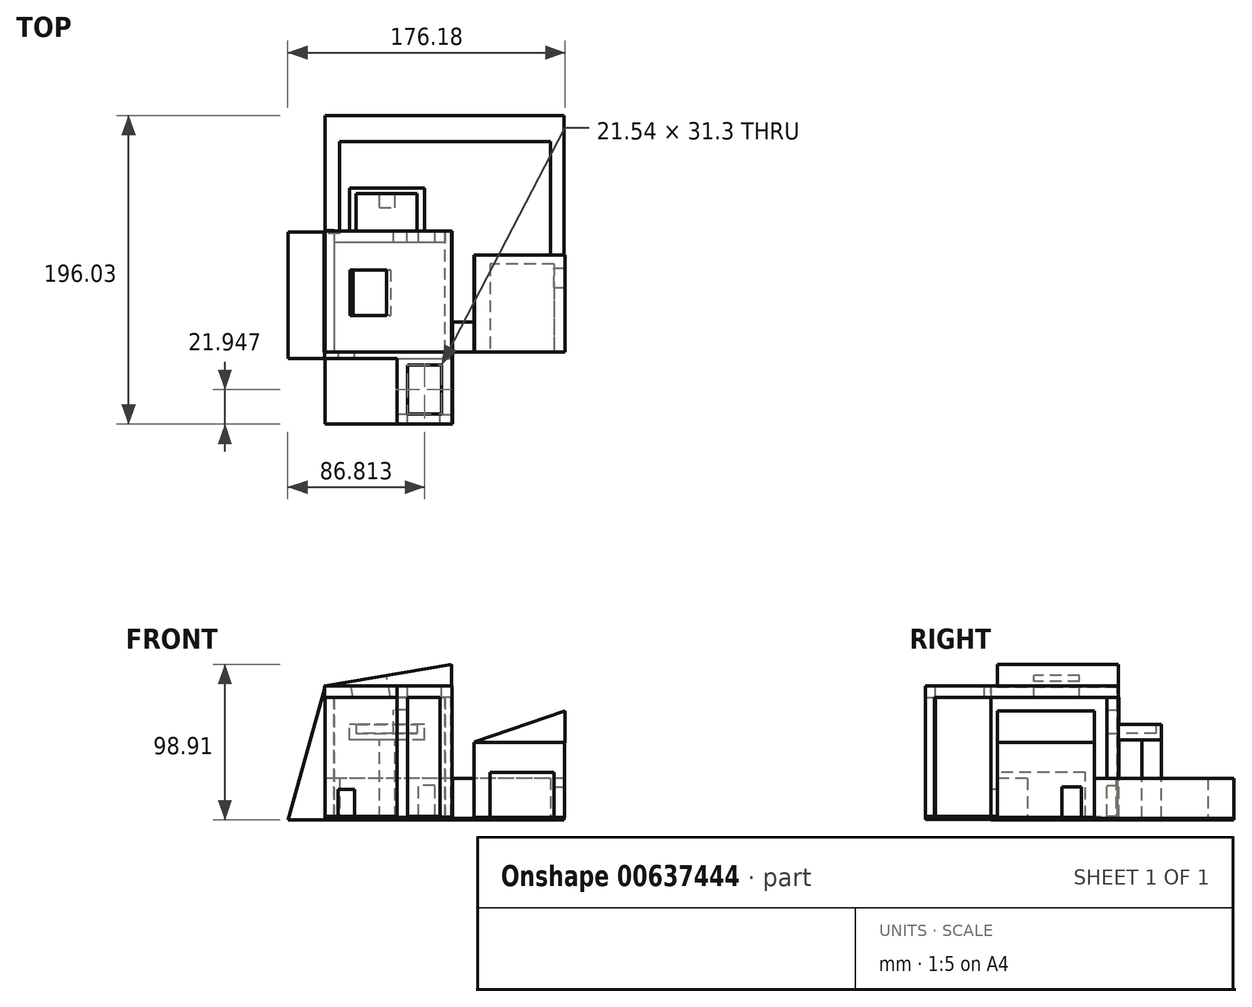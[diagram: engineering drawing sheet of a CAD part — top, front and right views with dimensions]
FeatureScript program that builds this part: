
annotation { "Feature Type Name" : "Feature", "Feature Type Description" : "" }
export const myFeature = defineFeature(function(context is Context, id is Id, definition is map)
    precondition{}
    {
        {
            var Q0;
            Q0=qCreatedBy(makeId("Front.planeOp"),FACE);
            var sketch = newSketch(context, id + "F0", { "sketchPlane" : qUnion([Q0])});
            skLineSegment(sketch, "E0.bottom", {"start": v(-75.95, -75.95) * mm, "end": v(21.4, -75.95) * mm});
            skLineSegment(sketch, "E0.top", {"start": v(-75.95, 0) * mm, "end": v(21.4, 0) * mm});
            skLineSegment(sketch, "E0.left", {"start": v(-75.95, -75.95) * mm, "end": v(-75.95, 0) * mm});
            skLineSegment(sketch, "E0.right", {"start": v(21.4, -75.95) * mm, "end": v(21.4, 0) * mm});
            skSolve(sketch);
        }
        {
            var Q0;
            Q0 = qSketchRegion(id + "F0", true);
            extrude(context, id + "F1", {"entities" : qUnion([Q0]), "depth" : 4.06 * mm, "offsetDistance" : 25.4 * mm});
        }
        {
            var Q0;
            Q0=qCreatedBy(makeId("Right.planeOp"),FACE);
            var sketch = newSketch(context, id + "F2", { "sketchPlane" : qUnion([Q0])});
            skLineSegment(sketch, "E1.bottom", {"start": v(0, 0) * mm, "end": v(76.87, 0) * mm});
            skLineSegment(sketch, "E1.top", {"start": v(0, -75.72) * mm, "end": v(76.87, -75.72) * mm});
            skLineSegment(sketch, "E1.left", {"start": v(0, 0) * mm, "end": v(0, -75.72) * mm});
            skLineSegment(sketch, "E1.right", {"start": v(76.87, 0) * mm, "end": v(76.87, -75.72) * mm});
            skSolve(sketch);
        }
        {
            var Q0;
            Q0=makeQuery(id+"F2.imprint","IMPRINT",FACE,{"disambiguationData":[TD([[makeQuery(id+"F2.imprint","IMPRINT",EDGE,{"derivedFrom":sQuery(id+"F2.wireOp",EDGE,"E1.bottom")}),-1.0]])]});
            extrude(context, id + "F3", {"entities" : qUnion([Q0]), "operationType" : NewBodyOperationType.ADD, "depth" : 4.06 * mm, "offsetDistance" : 25.4 * mm});
        }
        {
            var Q0;
            Q0=makeQuery(id+"F3.boolean.opBoolean","MERGE",FACE,{"derivedFrom":[makeQuery(id+"F1.opExtrude","SWEPT_FACE",FACE,{"disambiguationData":[OSD([sQuery(id+"F0.wireOp",EDGE,"E0.top")])]}),makeQuery(id+"F3.opExtrude","SWEPT_FACE",FACE,{"disambiguationData":[OSD([sQuery(id+"F2.wireOp",EDGE,"E1.bottom")])]})]});
            var sketch = newSketch(context, id + "F4", { "sketchPlane" : qUnion([Q0])});
            skLineSegment(sketch, "E2", {"start": v(4.06, 0) * mm, "end": v(4.06, -4.06) * mm});
            skLineSegment(sketch, "E3", {"start": v(4.06, -4.06) * mm, "end": v(21.4, -4.06) * mm});
            skLineSegment(sketch, "E4", {"start": v(21.4, -4.06) * mm, "end": v(21.4, 0) * mm});
            skLineSegment(sketch, "E5", {"start": v(21.4, 0) * mm, "end": v(4.06, 0) * mm});
            skSolve(sketch);
        }
        {
            var Q0;
            Q0=makeQuery(id+"F4.imprint","IMPRINT",FACE,{"disambiguationData":[TD([[makeQuery(id+"F4.imprint","IMPRINT",EDGE,{"derivedFrom":sQuery(id+"F4.wireOp",EDGE,"E2")}),1.0]])]});
            extrude(context, id + "F5", {"entities" : qUnion([Q0]), "operationType" : NewBodyOperationType.REMOVE, "oppositeDirection" : true, "depth" : 78.49 * mm, "offsetDistance" : 25.4 * mm});
        }
        {
            var Q0;
            Q0=qCreatedBy(makeId("Top.planeOp"),FACE);
            var sketch = newSketch(context, id + "F6", { "sketchPlane" : qUnion([Q0])});
            skLineSegment(sketch, "E6.bottom", {"start": v(4.07, 76.9) * mm, "end": v(-76, 76.9) * mm});
            skLineSegment(sketch, "E6.top", {"start": v(4.07, 69.6) * mm, "end": v(-76, 69.6) * mm});
            skLineSegment(sketch, "E6.left", {"start": v(4.07, 76.9) * mm, "end": v(4.07, 69.6) * mm});
            skLineSegment(sketch, "E6.right", {"start": v(-76, 76.9) * mm, "end": v(-76, 69.6) * mm});
            skSolve(sketch);
        }
        {
            var Q0;
            Q0=makeQuery(id+"F6.imprint","IMPRINT",FACE,{"disambiguationData":[TD([[makeQuery(id+"F6.imprint","IMPRINT",EDGE,{"derivedFrom":sQuery(id+"F6.wireOp",EDGE,"E6.bottom")}),1.0]])]});
            extrude(context, id + "F7", {"entities" : qUnion([Q0]), "operationType" : NewBodyOperationType.ADD, "oppositeDirection" : true, "depth" : 75.44 * mm, "offsetDistance" : 25.4 * mm});
        }
        {
            var Q0;
            Q0=makeQuery(id+"F1.opExtrude","CAP_FACE",FACE,{"disambiguationData":[OSD([sQuery(id+"F0.wireOp",EDGE,"E0.bottom"),sQuery(id+"F0.wireOp",EDGE,"E0.top"),sQuery(id+"F0.wireOp",EDGE,"E0.left"),sQuery(id+"F0.wireOp",EDGE,"E0.right")])],"isStart":false});
            var sketch = newSketch(context, id + "F8", { "sketchPlane" : qUnion([Q0])});
            skLineSegment(sketch, "E7.bottom", {"start": v(-67.84, -75.95) * mm, "end": v(-57.2, -75.95) * mm});
            skLineSegment(sketch, "E7.top", {"start": v(-67.84, -58.33) * mm, "end": v(-57.2, -58.33) * mm});
            skLineSegment(sketch, "E7.left", {"start": v(-67.84, -75.95) * mm, "end": v(-67.84, -58.33) * mm});
            skLineSegment(sketch, "E7.right", {"start": v(-57.2, -75.95) * mm, "end": v(-57.2, -58.33) * mm});
            skSolve(sketch);
        }
        {
            var Q0;
            Q0=makeQuery(id+"F8.imprint","IMPRINT",FACE,{"disambiguationData":[TD([[makeQuery(id+"F8.imprint","IMPRINT",EDGE,{"derivedFrom":sQuery(id+"F8.wireOp",EDGE,"E7.bottom")}),1.0]])]});
            extrude(context, id + "F9", {"entities" : qUnion([Q0]), "operationType" : NewBodyOperationType.REMOVE, "oppositeDirection" : true, "depth" : 25.4 * mm, "offsetDistance" : 25.4 * mm});
        }
        {
            var Q0;
            Q0=qCreatedBy(makeId("Top.planeOp"),FACE);
            var sketch = newSketch(context, id + "F10", { "sketchPlane" : qUnion([Q0])});
            skLineSegment(sketch, "E8.bottom", {"start": v(-76.3, 77.21) * mm, "end": v(-70.4, 77.21) * mm});
            skLineSegment(sketch, "E8.top", {"start": v(-76.3, -3.73) * mm, "end": v(-70.4, -3.73) * mm});
            skLineSegment(sketch, "E8.left", {"start": v(-76.3, 77.21) * mm, "end": v(-76.3, -3.73) * mm});
            skLineSegment(sketch, "E8.right", {"start": v(-70.4, 77.21) * mm, "end": v(-70.4, -3.73) * mm});
            skSolve(sketch);
        }
        {
            var Q0;
            Q0=makeQuery(id+"F10.imprint","IMPRINT",FACE,{"disambiguationData":[TD([[makeQuery(id+"F10.imprint","IMPRINT",EDGE,{"derivedFrom":sQuery(id+"F10.wireOp",EDGE,"E8.bottom")}),-1.0]])]});
            extrude(context, id + "F11", {"entities" : qUnion([Q0]), "operationType" : NewBodyOperationType.ADD, "oppositeDirection" : true, "depth" : 75.95 * mm, "offsetDistance" : 25.4 * mm});
        }
        {
            var Q0;
            Q0=qCreatedBy(makeId("Top.planeOp"),FACE);
            var sketch = newSketch(context, id + "F12", { "sketchPlane" : qUnion([Q0])});
            skLineSegment(sketch, "E9.bottom", {"start": v(-76.23, 76.97) * mm, "end": v(4.6, 76.97) * mm});
            skLineSegment(sketch, "E9.top", {"start": v(-76.23, -4.14) * mm, "end": v(4.6, -4.14) * mm});
            skLineSegment(sketch, "E9.left", {"start": v(-76.23, 76.97) * mm, "end": v(-76.23, -4.14) * mm});
            skLineSegment(sketch, "E9.right", {"start": v(4.6, 76.97) * mm, "end": v(4.6, -4.14) * mm});
            skSolve(sketch);
        }
        {
            var Q0;
            Q0=makeQuery(id+"F12.imprint","IMPRINT",FACE,{"disambiguationData":[TD([[makeQuery(id+"F12.imprint","IMPRINT",EDGE,{"derivedFrom":sQuery(id+"F12.wireOp",EDGE,"E9.bottom")}),-1.0]])]});
            extrude(context, id + "F13", {"entities" : qUnion([Q0]), "operationType" : NewBodyOperationType.ADD, "depth" : 7.37 * mm, "offsetDistance" : 25.4 * mm});
        }
        {
            var Q0;
            Q0=makeQuery(id+"F13.opExtrude","SWEPT_FACE",FACE,{"disambiguationData":[OSD([sQuery(id+"F12.wireOp",EDGE,"E9.top")])]});
            var sketch = newSketch(context, id + "F14", { "sketchPlane" : qUnion([Q0])});
            skLineSegment(sketch, "E10.bottom", {"start": v(-30.43, 7.37) * mm, "end": v(4.6, 7.37) * mm});
            skLineSegment(sketch, "E10.top", {"start": v(-30.43, 0) * mm, "end": v(4.6, 0) * mm});
            skLineSegment(sketch, "E10.left", {"start": v(-30.43, 7.37) * mm, "end": v(-30.43, 0) * mm});
            skLineSegment(sketch, "E10.right", {"start": v(4.6, 7.37) * mm, "end": v(4.6, 0) * mm});
            skSolve(sketch);
        }
        {
            var Q0;
            Q0=makeQuery(id+"F14.imprint","IMPRINT",FACE,{"disambiguationData":[TD([[makeQuery(id+"F14.imprint","IMPRINT",EDGE,{"derivedFrom":sQuery(id+"F14.wireOp",EDGE,"E10.bottom")}),-1.0]])]});
            extrude(context, id + "F15", {"entities" : qUnion([Q0]), "operationType" : NewBodyOperationType.ADD, "depth" : 41.66 * mm, "offsetDistance" : 25.4 * mm});
        }
        {
            var Q0;
            Q0=makeQuery(id+"F15.boolean.opBoolean","MERGE",FACE,{"derivedFrom":[makeQuery(id+"F13.opExtrude","CAP_FACE",FACE,{"disambiguationData":[OSD([sQuery(id+"F12.wireOp",EDGE,"E9.bottom"),sQuery(id+"F12.wireOp",EDGE,"E9.top"),sQuery(id+"F12.wireOp",EDGE,"E9.left"),sQuery(id+"F12.wireOp",EDGE,"E9.right")])],"isStart":false}),makeQuery(id+"F15.opExtrude","SWEPT_FACE",FACE,{"disambiguationData":[OSD([sQuery(id+"F14.wireOp",EDGE,"E10.bottom")])]})]});
            var sketch = newSketch(context, id + "F16", { "sketchPlane" : qUnion([Q0])});
            skLineSegment(sketch, "E11", {"start": v(-30.43, -4.14) * mm, "end": v(4.6, -4.14) * mm});
            skSolve(sketch);
        }
        {
            var Q0;
            {var subQ0=sQuery(id+"F16.wireOp",EDGE,"E11");Q0=makeQuery(id+"F16.imprint","IMPRINT",FACE,{"disambiguationData":[TD([[makeQuery(id+"F16.imprint","IMPRINT",EDGE,{"derivedFrom":subQ0}),-1.0]])]});}
            var sketch = newSketch(context, id + "F17", { "sketchPlane" : qUnion([Q0])});
            skLineSegment(sketch, "E12.bottom", {"start": v(-23.68, -8.2) * mm, "end": v(-2.14, -8.2) * mm});
            skLineSegment(sketch, "E12.top", {"start": v(-23.68, -39.5) * mm, "end": v(-2.14, -39.5) * mm});
            skLineSegment(sketch, "E12.left", {"start": v(-23.68, -8.2) * mm, "end": v(-23.68, -39.5) * mm});
            skLineSegment(sketch, "E12.right", {"start": v(-2.14, -8.2) * mm, "end": v(-2.14, -39.5) * mm});
            skSolve(sketch);
        }
        {
            var Q0;
            Q0=makeQuery(id+"F17.imprint","IMPRINT",FACE,{"disambiguationData":[TD([[makeQuery(id+"F17.imprint","IMPRINT",EDGE,{"derivedFrom":sQuery(id+"F17.wireOp",EDGE,"E12.bottom")}),-1.0]])]});
            extrude(context, id + "F18", {"entities" : qUnion([Q0]), "operationType" : NewBodyOperationType.REMOVE, "oppositeDirection" : true, "depth" : 25.4 * mm, "offsetDistance" : 25.4 * mm});
        }
        {
            var Q0;
            {var subQ2=sQuery(id+"F0.wireOp",EDGE,"E0.top");var subQ5=sQuery(id+"F12.wireOp",EDGE,"E9.top");var subQ7=sQuery(id+"F12.wireOp",EDGE,"E9.left");var subQ10=sQuery(id+"F12.wireOp",EDGE,"E9.bottom");var subQ11=sQuery(id+"F12.wireOp",EDGE,"E9.right");Q0=makeQuery(id+"F15.boolean.opBoolean","MERGE",FACE,{"derivedFrom":[makeQuery(id+"F13.boolean.opBoolean","SPLIT",FACE,{"disambiguationData":[TD([makeQuery(id+"F1.opExtrude","SWEPT_FACE",FACE,{"disambiguationData":[OSD([subQ2])]})])],"derivedFrom":makeQuery(id+"F13.opExtrude","CAP_FACE",FACE,{"disambiguationData":[OSD([subQ10,subQ5,subQ7,subQ11])],"isStart":true})}),makeQuery(id+"F15.opExtrude","SWEPT_FACE",FACE,{"disambiguationData":[OSD([sQuery(id+"F14.wireOp",EDGE,"E10.top")])]})]});}
            var sketch = newSketch(context, id + "F19", { "sketchPlane" : qUnion([Q0])});
            skLineSegment(sketch, "E13.bottom", {"start": v(-30.43, 45.8) * mm, "end": v(-23.68, 45.8) * mm});
            skLineSegment(sketch, "E13.top", {"start": v(-30.43, 39.5) * mm, "end": v(-23.68, 39.5) * mm});
            skLineSegment(sketch, "E13.left", {"start": v(-30.43, 45.8) * mm, "end": v(-30.43, 39.5) * mm});
            skLineSegment(sketch, "E13.right", {"start": v(-23.68, 45.8) * mm, "end": v(-23.68, 39.5) * mm});
            skSolve(sketch);
        }
        {
            var Q0;
            {var subQ26=sQuery(id+"F19.wireOp",EDGE,"E13.top");Q0=makeQuery(id+"F19.imprint","IMPRINT",FACE,{"disambiguationData":[TD([[makeQuery(id+"F19.imprint","IMPRINT",EDGE,{"derivedFrom":subQ26}),-1.0]])]});}
            var sketch = newSketch(context, id + "F20", { "sketchPlane" : qUnion([Q0])});
            skLineSegment(sketch, "E14.bottom", {"start": v(4.6, 45.82) * mm, "end": v(-3, 45.82) * mm});
            skLineSegment(sketch, "E14.top", {"start": v(4.6, 39.9) * mm, "end": v(-3, 39.9) * mm});
            skLineSegment(sketch, "E14.left", {"start": v(4.6, 45.82) * mm, "end": v(4.6, 39.9) * mm});
            skLineSegment(sketch, "E14.right", {"start": v(-3, 45.82) * mm, "end": v(-3, 39.9) * mm});
            skSolve(sketch);
        }
        {
            var Q0;
            Q0=makeQuery(id+"F19.imprint","IMPRINT",FACE,{"disambiguationData":[TD([[makeQuery(id+"F19.imprint","IMPRINT",EDGE,{"derivedFrom":sQuery(id+"F19.wireOp",EDGE,"E13.bottom")}),-1.0]])]});
            extrude(context, id + "F21", {"entities" : qUnion([Q0]), "operationType" : NewBodyOperationType.ADD, "depth" : 76.2 * mm, "offsetDistance" : 25.4 * mm});
        }
        {
            var Q0;
            {var subQ0=sQuery(id+"F20.wireOp",EDGE,"E14.top");Q0=makeQuery(id+"F20.imprint","IMPRINT",FACE,{"disambiguationData":[TD([[makeQuery(id+"F20.imprint","IMPRINT",EDGE,{"derivedFrom":subQ0}),-1.0]])]});}
            extrude(context, id + "F22", {"entities" : qUnion([Q0]), "operationType" : NewBodyOperationType.ADD, "depth" : 76.2 * mm, "offsetDistance" : 25.4 * mm});
        }
        {
            var Q0;
            Q0=qCreatedBy(makeId("Front.planeOp"),FACE);
            var sketch = newSketch(context, id + "F23", { "sketchPlane" : qUnion([Q0])});
            skLineSegment(sketch, "E15.bottom", {"start": v(75.9, -76.23) * mm, "end": v(18.55, -76.23) * mm});
            skLineSegment(sketch, "E15.top", {"start": v(75.9, -28.4) * mm, "end": v(18.55, -28.4) * mm});
            skLineSegment(sketch, "E15.left", {"start": v(75.9, -76.23) * mm, "end": v(75.9, -28.4) * mm});
            skLineSegment(sketch, "E15.right", {"start": v(18.55, -76.23) * mm, "end": v(18.55, -28.4) * mm});
            skSolve(sketch);
        }
        {
            var Q0;
            Q0=qCreatedBy(makeId("Front.planeOp"),FACE);
            var sketch = newSketch(context, id + "F24", { "sketchPlane" : qUnion([Q0])});
            skLineSegment(sketch, "E16", {"start": v(18.83, -28.12) * mm, "end": v(76.46, -8.53) * mm});
            skLineSegment(sketch, "E17", {"start": v(76.46, -8.53) * mm, "end": v(76.46, -28.4) * mm});
            skLineSegment(sketch, "E18", {"start": v(76.46, -28.4) * mm, "end": v(18.83, -28.12) * mm});
            skSolve(sketch);
        }
        {
            var Q0;
            Q0=makeQuery(id+"F24.imprint","IMPRINT",FACE,{"disambiguationData":[TD([[makeQuery(id+"F24.imprint","IMPRINT",EDGE,{"derivedFrom":sQuery(id+"F24.wireOp",EDGE,"E16")}),-1.0]])]});
            extrude(context, id + "F25", {"entities" : qUnion([Q0]), "oppositeDirection" : true, "depth" : 61.47 * mm, "offsetDistance" : 25.4 * mm});
        }
        {
            var Q0;
            Q0=makeQuery(id+"F23.imprint","IMPRINT",FACE,{"disambiguationData":[TD([[makeQuery(id+"F23.imprint","IMPRINT",EDGE,{"derivedFrom":sQuery(id+"F23.wireOp",EDGE,"E15.bottom")}),-1.0]])]});
            extrude(context, id + "F26", {"entities" : qUnion([Q0]), "oppositeDirection" : true, "depth" : 61.47 * mm, "offsetDistance" : 25.4 * mm});
        }
        {
            var Q0;
            Q0=makeQuery(id+"F26.opExtrude","CAP_FACE",FACE,{"disambiguationData":[OSD([sQuery(id+"F23.wireOp",EDGE,"E15.bottom"),sQuery(id+"F23.wireOp",EDGE,"E15.top"),sQuery(id+"F23.wireOp",EDGE,"E15.left"),sQuery(id+"F23.wireOp",EDGE,"E15.right")])],"isStart":true});
            var sketch = newSketch(context, id + "F27", { "sketchPlane" : qUnion([Q0])});
            skLineSegment(sketch, "E19.bottom", {"start": v(28.76, -76.23) * mm, "end": v(69.33, -76.23) * mm});
            skLineSegment(sketch, "E19.top", {"start": v(28.76, -47.73) * mm, "end": v(69.33, -47.73) * mm});
            skLineSegment(sketch, "E19.left", {"start": v(28.76, -76.23) * mm, "end": v(28.76, -47.73) * mm});
            skLineSegment(sketch, "E19.right", {"start": v(69.33, -76.23) * mm, "end": v(69.33, -47.73) * mm});
            skSolve(sketch);
        }
        {
            var Q0;
            Q0=makeQuery(id+"F27.imprint","IMPRINT",FACE,{"disambiguationData":[TD([[makeQuery(id+"F27.imprint","IMPRINT",EDGE,{"derivedFrom":sQuery(id+"F27.wireOp",EDGE,"E19.bottom")}),-1.0]])]});
            extrude(context, id + "F28", {"entities" : qUnion([Q0]), "operationType" : NewBodyOperationType.REMOVE, "oppositeDirection" : true, "depth" : 55.88 * mm, "offsetDistance" : 25.4 * mm});
        }
        {
            var Q0;
            Q0=makeQuery(id+"F26.opExtrude","SWEPT_FACE",FACE,{"disambiguationData":[OSD([sQuery(id+"F23.wireOp",EDGE,"E15.left")])]});
            var sketch = newSketch(context, id + "F29", { "sketchPlane" : qUnion([Q0])});
            skLineSegment(sketch, "E20.bottom", {"start": v(40.94, -76.23) * mm, "end": v(53.25, -76.23) * mm});
            skLineSegment(sketch, "E20.top", {"start": v(40.94, -56.68) * mm, "end": v(53.25, -56.68) * mm});
            skLineSegment(sketch, "E20.left", {"start": v(40.94, -76.23) * mm, "end": v(40.94, -56.68) * mm});
            skLineSegment(sketch, "E20.right", {"start": v(53.25, -76.23) * mm, "end": v(53.25, -56.68) * mm});
            skSolve(sketch);
        }
        {
            var Q0;
            Q0=makeQuery(id+"F29.imprint","IMPRINT",FACE,{"disambiguationData":[TD([[makeQuery(id+"F29.imprint","IMPRINT",EDGE,{"derivedFrom":sQuery(id+"F29.wireOp",EDGE,"E20.bottom")}),-1.0]])]});
            extrude(context, id + "F30", {"entities" : qUnion([Q0]), "operationType" : NewBodyOperationType.REMOVE, "oppositeDirection" : true, "depth" : 25.4 * mm, "offsetDistance" : 25.4 * mm});
        }
        {
            var Q0;
            {var subQ1=sQuery(id+"F0.wireOp",EDGE,"E0.left");var subQ3=sQuery(id+"F0.wireOp",EDGE,"E0.bottom");Q0=makeQuery(id+"F9.boolean.opBoolean","SPLIT",FACE,{"disambiguationData":[TD([makeQuery(id+"F1.opExtrude","SWEPT_FACE",FACE,{"disambiguationData":[OSD([subQ1])]})])],"derivedFrom":makeQuery(id+"F1.opExtrude","SWEPT_FACE",FACE,{"disambiguationData":[OSD([subQ3])]})});}
            var sketch = newSketch(context, id + "F31", { "sketchPlane" : qUnion([Q0])});
            skLineSegment(sketch, "E21.bottom", {"start": v(-75.95, 0) * mm, "end": v(4.91, 0) * mm});
            skLineSegment(sketch, "E21.top", {"start": v(-75.95, 45.65) * mm, "end": v(4.91, 45.65) * mm});
            skLineSegment(sketch, "E21.left", {"start": v(-75.95, 0) * mm, "end": v(-75.95, 45.65) * mm});
            skLineSegment(sketch, "E21.right", {"start": v(4.91, 0) * mm, "end": v(4.91, 45.65) * mm});
            skSolve(sketch);
        }
        {
            var Q0;
            {var subQ6=sQuery(id+"F31.wireOp",EDGE,"E21.top");Q0=makeQuery(id+"F31.imprint","IMPRINT",FACE,{"disambiguationData":[TD([[makeQuery(id+"F31.imprint","IMPRINT",EDGE,{"derivedFrom":subQ6}),-1.0]])]});}
            extrude(context, id + "F32", {"entities" : qUnion([Q0]), "operationType" : NewBodyOperationType.ADD, "depth" : 1.52 * mm, "offsetDistance" : 25.4 * mm, "hasSecondDirection" : true, "secondDirectionOppositeDirection" : true, "secondDirectionDepth" : 0.5 * mm});
        }
        {
            var Q0;
            {var subQ0=sQuery(id+"F23.wireOp",EDGE,"E15.right");var subQ5=sQuery(id+"F23.wireOp",EDGE,"E15.bottom");Q0=makeQuery(id+"F30.boolean.opBoolean","SPLIT",FACE,{"disambiguationData":[TD([makeQuery(id+"F26.opExtrude","SWEPT_FACE",FACE,{"disambiguationData":[OSD([subQ0])]})])],"derivedFrom":makeQuery(id+"F26.opExtrude","SWEPT_FACE",FACE,{"disambiguationData":[OSD([subQ5])]})});}
            var sketch = newSketch(context, id + "F33", { "sketchPlane" : qUnion([Q0])});
            skLineSegment(sketch, "E22.bottom", {"start": v(75.8, 0) * mm, "end": v(-76.13, 0) * mm});
            skLineSegment(sketch, "E22.top", {"start": v(75.8, -150.23) * mm, "end": v(-76.13, -150.23) * mm});
            skLineSegment(sketch, "E22.left", {"start": v(75.8, 0) * mm, "end": v(75.8, -150.23) * mm});
            skLineSegment(sketch, "E22.right", {"start": v(-76.13, 0) * mm, "end": v(-76.13, -150.23) * mm});
            skSolve(sketch);
        }
        {
            var Q0;
            {var subQ1=sQuery(id+"F33.wireOp",EDGE,"E22.top");Q0=makeQuery(id+"F33.imprint","IMPRINT",FACE,{"disambiguationData":[TD([[makeQuery(id+"F33.imprint","IMPRINT",EDGE,{"derivedFrom":subQ1}),-1.0]])]});}
            extrude(context, id + "F34", {"entities" : qUnion([Q0]), "operationType" : NewBodyOperationType.ADD, "depth" : 1.52 * mm, "offsetDistance" : 25.4 * mm, "hasSecondDirection" : true, "secondDirectionOppositeDirection" : false, "secondDirectionDepth" : 0.5 * mm});
        }
        {
            var Q0;
            Q0=makeQuery(id+"F34.opExtrude","CAP_FACE",FACE,{"disambiguationData":[OSD([sQuery(id+"F23.wireOp",EDGE,"E15.bottom"),sQuery(id+"F23.wireOp",EDGE,"E15.right"),sQuery(id+"F33.wireOp",EDGE,"E22.bottom"),sQuery(id+"F33.wireOp",EDGE,"E22.top"),sQuery(id+"F33.wireOp",EDGE,"E22.left"),sQuery(id+"F33.wireOp",EDGE,"E22.right")])],"isStart":true});
            var sketch = newSketch(context, id + "F35", { "sketchPlane" : qUnion([Q0])});
            skLineSegment(sketch, "E23", {"start": v(75.8, 61.47) * mm, "end": v(67.06, 61.47) * mm});
            skLineSegment(sketch, "E24", {"start": v(67.06, 61.47) * mm, "end": v(67.06, 133.69) * mm});
            skLineSegment(sketch, "E25", {"start": v(67.06, 133.69) * mm, "end": v(-66.76, 133.69) * mm});
            skLineSegment(sketch, "E26", {"start": v(-66.76, 133.69) * mm, "end": v(-66.76, 75.27) * mm});
            skLineSegment(sketch, "E27", {"start": v(-66.76, 75.27) * mm, "end": v(-76.13, 75.27) * mm});
            skLineSegment(sketch, "E28", {"start": v(-76.13, 75.27) * mm, "end": v(-76.13, 150.23) * mm});
            skLineSegment(sketch, "E29", {"start": v(-76.13, 150.23) * mm, "end": v(75.8, 150.23) * mm});
            skLineSegment(sketch, "E30", {"start": v(75.8, 150.23) * mm, "end": v(75.8, 61.47) * mm});
            skSolve(sketch);
        }
        {
            var Q0;
            Q0=makeQuery(id+"F35.imprint","IMPRINT",FACE,{"disambiguationData":[TD([[makeQuery(id+"F35.imprint","IMPRINT",EDGE,{"derivedFrom":sQuery(id+"F35.wireOp",EDGE,"E23")}),-1.0]])]});
            extrude(context, id + "F36", {"entities" : qUnion([Q0]), "depth" : 25.4 * mm, "offsetDistance" : 25.4 * mm});
        }
        {
            var Q0;
            Q0=makeQuery(id+"F7.opExtrude","SWEPT_FACE",FACE,{"disambiguationData":[OSD([sQuery(id+"F6.wireOp",EDGE,"E6.bottom")])]});
            var sketch = newSketch(context, id + "F37", { "sketchPlane" : qUnion([Q0])});
            skLineSegment(sketch, "E31.bottom", {"start": v(6.37, -75.44) * mm, "end": v(16.83, -75.44) * mm});
            skLineSegment(sketch, "E31.top", {"start": v(6.37, -55.91) * mm, "end": v(16.83, -55.91) * mm});
            skLineSegment(sketch, "E31.left", {"start": v(6.37, -75.44) * mm, "end": v(6.37, -55.91) * mm});
            skLineSegment(sketch, "E31.right", {"start": v(16.83, -75.44) * mm, "end": v(16.83, -55.91) * mm});
            skSolve(sketch);
        }
        {
            var Q0;
            Q0=makeQuery(id+"F37.imprint","IMPRINT",FACE,{"disambiguationData":[TD([[makeQuery(id+"F37.imprint","IMPRINT",EDGE,{"derivedFrom":sQuery(id+"F37.wireOp",EDGE,"E31.bottom")}),1.0]])]});
            extrude(context, id + "F38", {"entities" : qUnion([Q0]), "operationType" : NewBodyOperationType.REMOVE, "oppositeDirection" : true, "depth" : 25.4 * mm, "offsetDistance" : 25.4 * mm});
        }
        {
            var Q0;
            Q0=makeQuery(id+"F34.opExtrude","CAP_FACE",FACE,{"disambiguationData":[OSD([sQuery(id+"F23.wireOp",EDGE,"E15.bottom"),sQuery(id+"F23.wireOp",EDGE,"E15.right"),sQuery(id+"F33.wireOp",EDGE,"E22.bottom"),sQuery(id+"F33.wireOp",EDGE,"E22.top"),sQuery(id+"F33.wireOp",EDGE,"E22.left"),sQuery(id+"F33.wireOp",EDGE,"E22.right")])],"isStart":true});
            var sketch = newSketch(context, id + "F39", { "sketchPlane" : qUnion([Q0])});
            skLineSegment(sketch, "E32", {"start": v(4.86, 18.93) * mm, "end": v(18.55, 18.93) * mm});
            skLineSegment(sketch, "E33", {"start": v(4.86, 18.93) * mm, "end": v(4.91, 0) * mm});
            skLineSegment(sketch, "E34", {"start": v(4.91, 0) * mm, "end": v(18.55, 0) * mm});
            skLineSegment(sketch, "E35", {"start": v(18.55, 0) * mm, "end": v(18.55, 18.93) * mm});
            skSolve(sketch);
        }
        {
            var Q0;
            Q0=makeQuery(id+"F39.imprint","IMPRINT",FACE,{"disambiguationData":[TD([[makeQuery(id+"F39.imprint","IMPRINT",EDGE,{"derivedFrom":sQuery(id+"F39.wireOp",EDGE,"E32")}),-1.0]])]});
            extrude(context, id + "F40", {"entities" : qUnion([Q0]), "depth" : 25.4 * mm, "offsetDistance" : 25.4 * mm});
        }
        {
            var Q0;
            Q0=qCreatedBy(makeId("Front.planeOp"),FACE);
            var sketch = newSketch(context, id + "F41", { "sketchPlane" : qUnion([Q0])});
            skLineSegment(sketch, "E36", {"start": v(-76.65, 7.28) * mm, "end": v(4.18, 21.12) * mm});
            skLineSegment(sketch, "E37", {"start": v(4.18, 21.12) * mm, "end": v(4.18, 6.43) * mm});
            skLineSegment(sketch, "E38", {"start": v(4.18, 6.43) * mm, "end": v(-76.65, 7.28) * mm});
            skSolve(sketch);
        }
        {
            var Q0;
            Q0=makeQuery(id+"F41.imprint","IMPRINT",FACE,{"disambiguationData":[TD([[makeQuery(id+"F41.imprint","IMPRINT",EDGE,{"derivedFrom":sQuery(id+"F41.wireOp",EDGE,"E36")}),-1.0]])]});
            extrude(context, id + "F42", {"entities" : qUnion([Q0]), "operationType" : NewBodyOperationType.ADD, "oppositeDirection" : true, "depth" : 76.96 * mm, "offsetDistance" : 25.4 * mm});
        }
        {
            var Q0;
            {var subQ2=sQuery(id+"F41.wireOp",EDGE,"E37");var subQ3=sQuery(id+"F41.wireOp",EDGE,"E36");Q0=makeQuery(id+"F42.boolean.opBoolean","SPLIT",FACE,{"disambiguationData":[TD([makeQuery(id+"F42.opExtrude","SWEPT_FACE",FACE,{"disambiguationData":[OSD([subQ2])]})])],"derivedFrom":makeQuery(id+"F42.opExtrude","SWEPT_FACE",FACE,{"disambiguationData":[OSD([subQ3])]})});}
            var sketch = newSketch(context, id + "F43", { "sketchPlane" : qUnion([Q0])});
            skLineSegment(sketch, "E39.bottom", {"start": v(-57.53, 52.22) * mm, "end": v(-34.11, 52.22) * mm});
            skLineSegment(sketch, "E39.top", {"start": v(-57.53, 23.31) * mm, "end": v(-34.11, 23.31) * mm});
            skLineSegment(sketch, "E39.left", {"start": v(-57.53, 52.22) * mm, "end": v(-57.53, 23.31) * mm});
            skLineSegment(sketch, "E39.right", {"start": v(-34.11, 52.22) * mm, "end": v(-34.11, 23.31) * mm});
            skSolve(sketch);
        }
        {
            var Q0;
            Q0=makeQuery(id+"F43.imprint","IMPRINT",FACE,{"disambiguationData":[TD([[makeQuery(id+"F43.imprint","IMPRINT",EDGE,{"derivedFrom":sQuery(id+"F43.wireOp",EDGE,"E39.bottom")}),-1.0]])]});
            extrude(context, id + "F44", {"entities" : qUnion([Q0]), "operationType" : NewBodyOperationType.REMOVE, "oppositeDirection" : true, "depth" : 25.4 * mm, "offsetDistance" : 25.4 * mm});
        }
        {
            var Q0;
            Q0=makeQuery(id+"F7.opExtrude","SWEPT_FACE",FACE,{"disambiguationData":[OSD([sQuery(id+"F6.wireOp",EDGE,"E6.bottom")])]});
            var sketch = newSketch(context, id + "F45", { "sketchPlane" : qUnion([Q0])});
            skLineSegment(sketch, "E40.bottom", {"start": v(12.95, -26.92) * mm, "end": v(60.43, -26.92) * mm});
            skLineSegment(sketch, "E40.top", {"start": v(12.95, -22.68) * mm, "end": v(60.43, -22.68) * mm});
            skLineSegment(sketch, "E40.left", {"start": v(12.95, -26.92) * mm, "end": v(12.95, -22.68) * mm});
            skLineSegment(sketch, "E40.right", {"start": v(60.43, -26.92) * mm, "end": v(60.43, -22.68) * mm});
            skSolve(sketch);
        }
        {
            var Q0;
            Q0=makeQuery(id+"F45.imprint","IMPRINT",FACE,{"disambiguationData":[TD([[makeQuery(id+"F45.imprint","IMPRINT",EDGE,{"derivedFrom":sQuery(id+"F45.wireOp",EDGE,"E40.bottom")}),1.0]])]});
            extrude(context, id + "F46", {"entities" : qUnion([Q0]), "operationType" : NewBodyOperationType.ADD, "depth" : 27.18 * mm, "offsetDistance" : 25.4 * mm});
        }
        {
            var Q0;
            Q0=makeQuery(id+"F46.opExtrude","SWEPT_FACE",FACE,{"disambiguationData":[OSD([sQuery(id+"F45.wireOp",EDGE,"E40.top")])]});
            var sketch = newSketch(context, id + "F47", { "sketchPlane" : qUnion([Q0])});
            skLineSegment(sketch, "E41", {"start": v(-56.41, 76.9) * mm, "end": v(-56.41, 100.82) * mm});
            skLineSegment(sketch, "E42", {"start": v(-56.41, 100.82) * mm, "end": v(-17.76, 100.82) * mm});
            skLineSegment(sketch, "E43", {"start": v(-17.76, 100.82) * mm, "end": v(-17.76, 76.9) * mm});
            skSolve(sketch);
        }
        {
            var Q0;
            {var subQ3=sQuery(id+"F47.wireOp",EDGE,"E41");Q0=makeQuery(id+"F47.imprint","IMPRINT",FACE,{"disambiguationData":[TD([[makeQuery(id+"F47.imprint","IMPRINT",EDGE,{"derivedFrom":subQ3}),1.0]])]});}
            extrude(context, id + "F48", {"entities" : qUnion([Q0]), "operationType" : NewBodyOperationType.ADD, "depth" : 5.6 * mm, "offsetDistance" : 25.4 * mm});
        }
        {
            var Q0;
            Q0=makeQuery(id+"F7.opExtrude","SWEPT_FACE",FACE,{"disambiguationData":[OSD([sQuery(id+"F6.wireOp",EDGE,"E6.bottom")])]});
            var sketch = newSketch(context, id + "F49", { "sketchPlane" : qUnion([Q0])});
            skLineSegment(sketch, "E44.bottom", {"start": v(23.98, -22.68) * mm, "end": v(32.52, -22.68) * mm});
            skLineSegment(sketch, "E44.top", {"start": v(23.98, -7.89) * mm, "end": v(32.52, -7.89) * mm});
            skLineSegment(sketch, "E44.left", {"start": v(23.98, -22.68) * mm, "end": v(23.98, -7.89) * mm});
            skLineSegment(sketch, "E44.right", {"start": v(32.52, -22.68) * mm, "end": v(32.52, -7.89) * mm});
            skSolve(sketch);
        }
        {
            var Q0;
            Q0=makeQuery(id+"F49.imprint","IMPRINT",FACE,{"disambiguationData":[TD([[makeQuery(id+"F49.imprint","IMPRINT",EDGE,{"derivedFrom":sQuery(id+"F49.wireOp",EDGE,"E44.bottom")}),1.0]])]});
            extrude(context, id + "F50", {"entities" : qUnion([Q0]), "operationType" : NewBodyOperationType.REMOVE, "oppositeDirection" : true, "depth" : 25.4 * mm, "offsetDistance" : 25.4 * mm});
        }
        {
            var Q0;
            Q0=makeQuery(id+"F1.opExtrude","CAP_FACE",FACE,{"disambiguationData":[OSD([sQuery(id+"F0.wireOp",EDGE,"E0.bottom"),sQuery(id+"F0.wireOp",EDGE,"E0.top"),sQuery(id+"F0.wireOp",EDGE,"E0.left"),sQuery(id+"F0.wireOp",EDGE,"E0.right")])],"isStart":false});
            var sketch = newSketch(context, id + "F51", { "sketchPlane" : qUnion([Q0])});
            skLineSegment(sketch, "E45", {"start": v(-75.95, -77.8) * mm, "end": v(-99.72, -77.8) * mm});
            skLineSegment(sketch, "E46", {"start": v(-99.72, -77.8) * mm, "end": v(-75.95, 6.43) * mm});
            skLineSegment(sketch, "E47", {"start": v(-75.95, 6.43) * mm, "end": v(-75.95, -77.8) * mm});
            skSolve(sketch);
        }
        {
            var Q0;
            {var subQ4=sQuery(id+"F51.wireOp",EDGE,"E45");Q0=makeQuery(id+"F51.imprint","IMPRINT",FACE,{"disambiguationData":[TD([[makeQuery(id+"F51.imprint","IMPRINT",EDGE,{"derivedFrom":subQ4}),-1.0]])]});}
            extrude(context, id + "F52", {"entities" : qUnion([Q0]), "oppositeDirection" : true, "depth" : 80.26 * mm, "offsetDistance" : 25.4 * mm});
        }
        {
            var Q0;
            Q0=makeQuery(id+"F46.opExtrude","SWEPT_FACE",FACE,{"disambiguationData":[OSD([sQuery(id+"F45.wireOp",EDGE,"E40.bottom")])]});
            var sketch = newSketch(context, id + "F53", { "sketchPlane" : qUnion([Q0])});
            skLineSegment(sketch, "E48.bottom", {"start": v(-31.47, -104.08) * mm, "end": v(-41.5, -104.08) * mm});
            skLineSegment(sketch, "E48.top", {"start": v(-31.47, -91.9) * mm, "end": v(-41.5, -91.9) * mm});
            skLineSegment(sketch, "E48.left", {"start": v(-31.47, -104.08) * mm, "end": v(-31.47, -91.9) * mm});
            skLineSegment(sketch, "E48.right", {"start": v(-41.5, -104.08) * mm, "end": v(-41.5, -91.9) * mm});
            skSolve(sketch);
        }
        {
            var Q0;
            Q0=makeQuery(id+"F53.imprint","IMPRINT",FACE,{"disambiguationData":[TD([[makeQuery(id+"F53.imprint","IMPRINT",EDGE,{"derivedFrom":sQuery(id+"F53.wireOp",EDGE,"E48.bottom")}),-1.0]])]});
            extrude(context, id + "F54", {"entities" : qUnion([Q0]), "operationType" : NewBodyOperationType.ADD, "depth" : 50.55 * mm, "offsetDistance" : 25.4 * mm});
        }
    });
